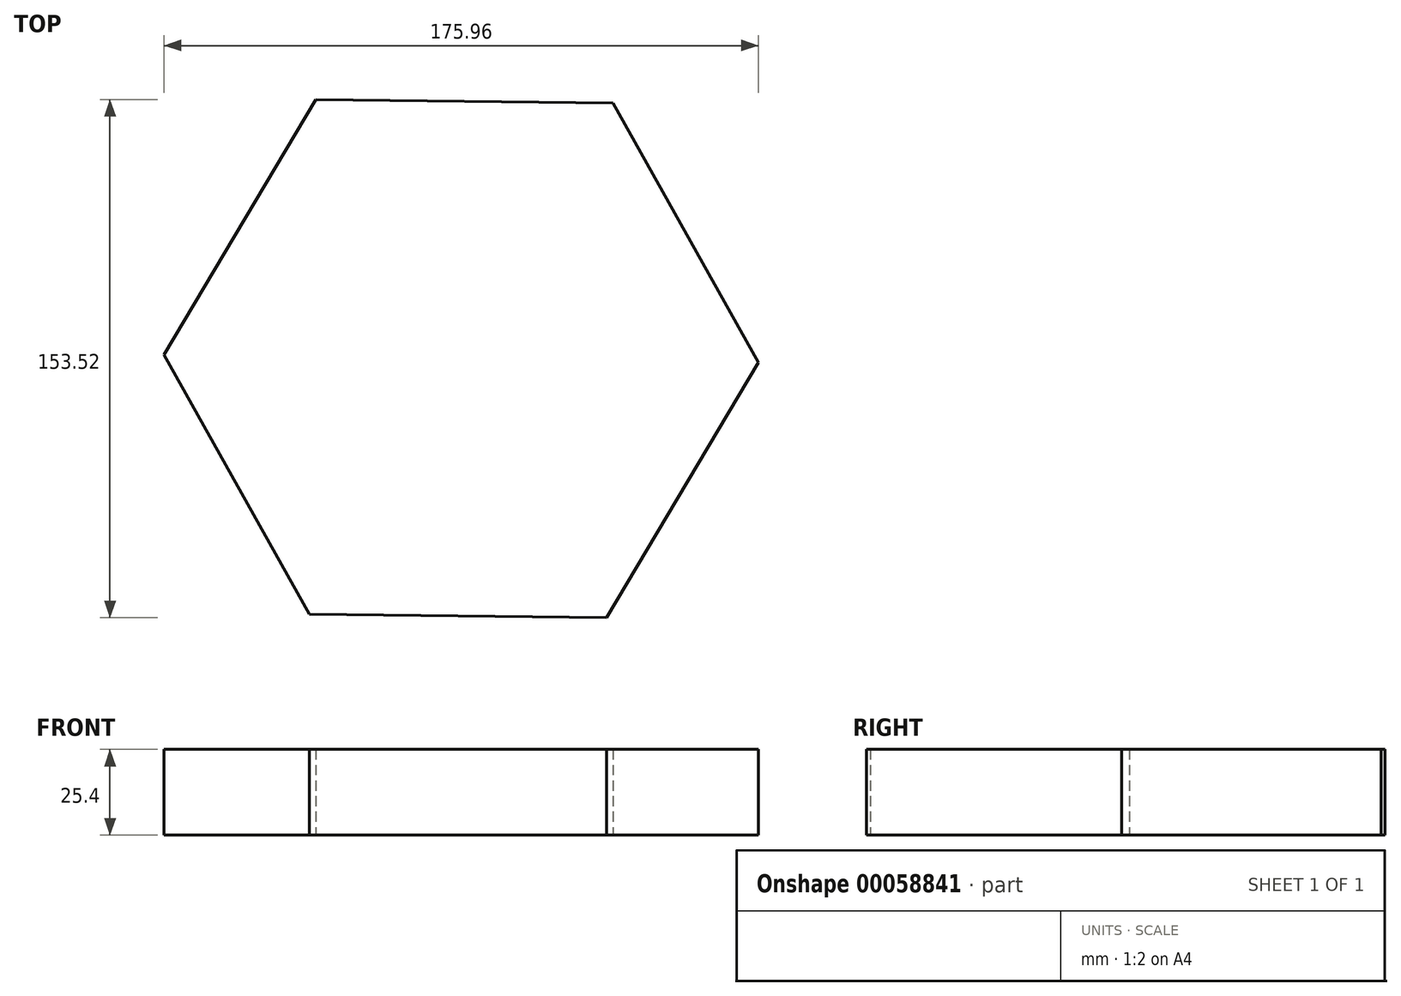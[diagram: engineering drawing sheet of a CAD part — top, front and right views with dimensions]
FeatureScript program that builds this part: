
annotation { "Feature Type Name" : "Feature", "Feature Type Description" : "" }
export const myFeature = defineFeature(function(context is Context, id is Id, definition is map)
    precondition{}
    {
        {
            var Q0;
            Q0=qCreatedBy(makeId("Top.planeOp"),FACE);
            var sketch = newSketch(context, id + "F0", { "sketchPlane" : qUnion([Q0])});
            skCircle(sketch, "E0.cCircle", {"center": v(0, 0) * mm, "radius": 76.2 * mm, "construction": true});
            skLineSegment(sketch, "E0.0", {"start": v(-43.02, 76.76) * mm, "end": v(44.97, 75.63) * mm});
            skLineSegment(sketch, "E0.1", {"start": v(44.97, 75.63) * mm, "end": v(87.98, -1.13) * mm});
            skLineSegment(sketch, "E0.2", {"start": v(87.98, -1.13) * mm, "end": v(43.02, -76.76) * mm});
            skLineSegment(sketch, "E0.3", {"start": v(43.02, -76.76) * mm, "end": v(-44.97, -75.63) * mm});
            skLineSegment(sketch, "E0.4", {"start": v(-44.97, -75.63) * mm, "end": v(-87.98, 1.13) * mm});
            skLineSegment(sketch, "E0.5", {"start": v(-87.98, 1.13) * mm, "end": v(-43.02, 76.76) * mm});
            skPoint(sketch, "E0.0.midPoint", {"position": v(0.98, 76.2) * mm});
            skSolve(sketch);
        }
        {
            var Q0;
            Q0=makeQuery(id+"F0.imprint","IMPRINT",FACE,{"disambiguationData":[TD([[makeQuery(id+"F0.imprint","IMPRINT",EDGE,{"derivedFrom":sQuery(id+"F0.wireOp",EDGE,"E0.0")}),-1.0]])]});
            extrude(context, id + "F1", {"entities" : qUnion([Q0]), "depth" : 25.4 * mm});
        }
    });
